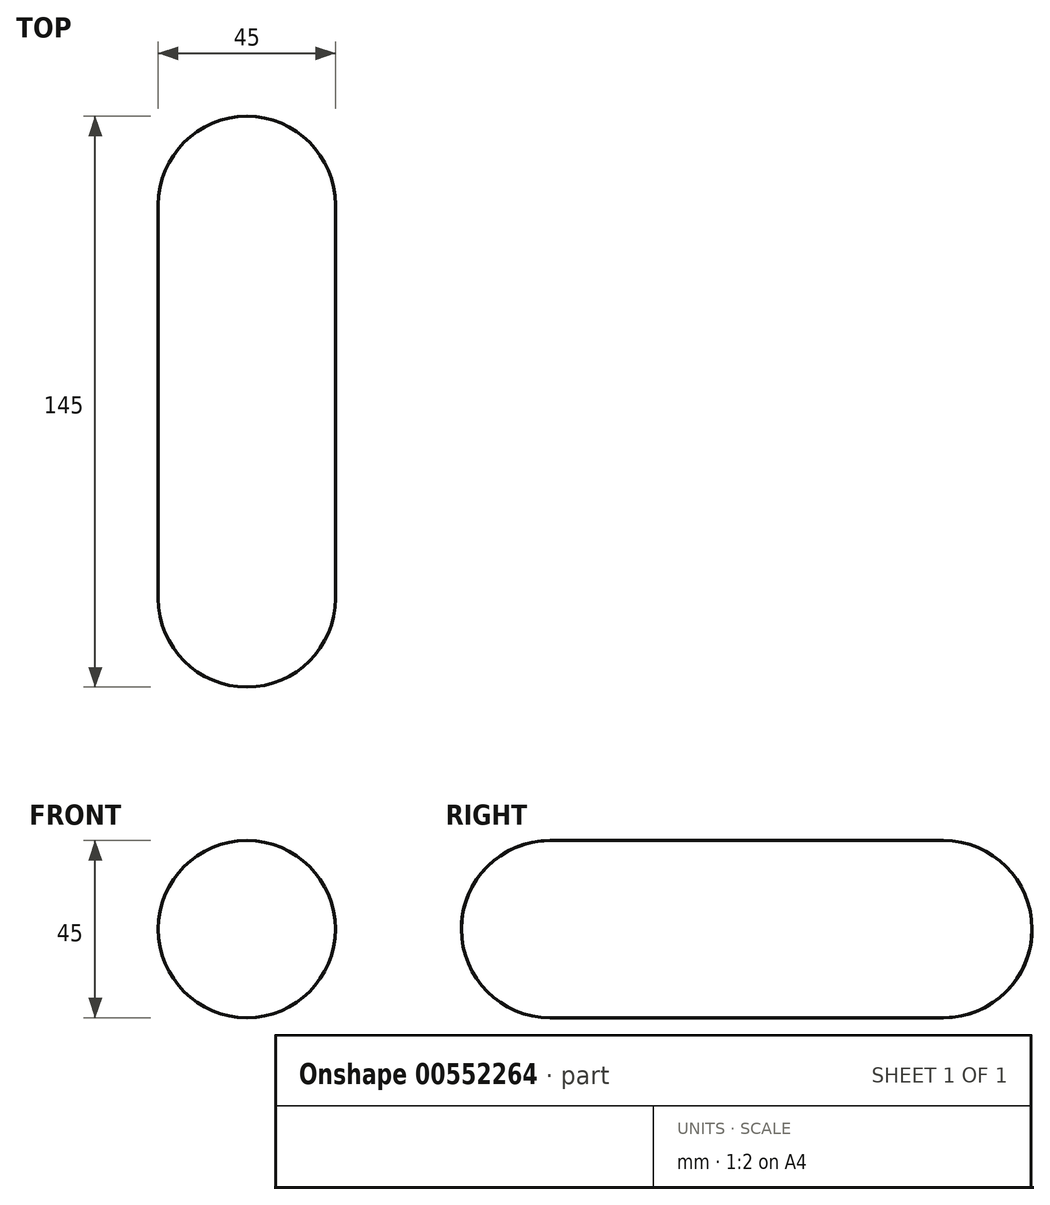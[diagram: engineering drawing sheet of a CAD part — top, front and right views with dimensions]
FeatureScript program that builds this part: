
annotation { "Feature Type Name" : "Feature", "Feature Type Description" : "" }
export const myFeature = defineFeature(function(context is Context, id is Id, definition is map)
    precondition{}
    {
        {
            var Q0;
            Q0=qCreatedBy(makeId("Right.planeOp"),FACE);
            var sketch = newSketch(context, id + "F0", { "sketchPlane" : qUnion([Q0])});
            skLineSegment(sketch, "E0", {"start": v(-50, 0) * mm, "end": v(50, 0) * mm, "construction": true});
            skArc(sketch, "E1", {"start": v(-50, 22.5) * mm, "mid": v(-72.5, 0) * mm, "end": v(-50, -22.5) * mm});
            skArc(sketch, "E2", {"start": v(50, -22.5) * mm, "mid": v(72.5, 0) * mm, "end": v(50, 22.5) * mm});
            skLineSegment(sketch, "E3", {"start": v(-50, 22.5) * mm, "end": v(50, 22.5) * mm});
            skLineSegment(sketch, "E4", {"start": v(-50, -22.5) * mm, "end": v(50, -22.5) * mm});
            skLineSegment(sketch, "E5", {"start": v(-72.5, 0) * mm, "end": v(72.5, 0) * mm});
            skSolve(sketch);
        }
        {
            var Q0;
            {var subQ0=sQuery(id+"F0.wireOp",EDGE,"E3");Q0=makeQuery(id+"F0.imprint","IMPRINT",FACE,{"disambiguationData":[TD([[makeQuery(id+"F0.imprint","IMPRINT",EDGE,{"derivedFrom":subQ0}),-1.0]])]});}
            var Q1;
            Q1=sQuery(id+"F0.wireOp",EDGE,"E5");
            revolve(context, id + "F1", {"entities" : qUnion([Q0]), "axis" : qUnion([Q1]), "revolveType" : RevolveType.FULL});
        }
    });
